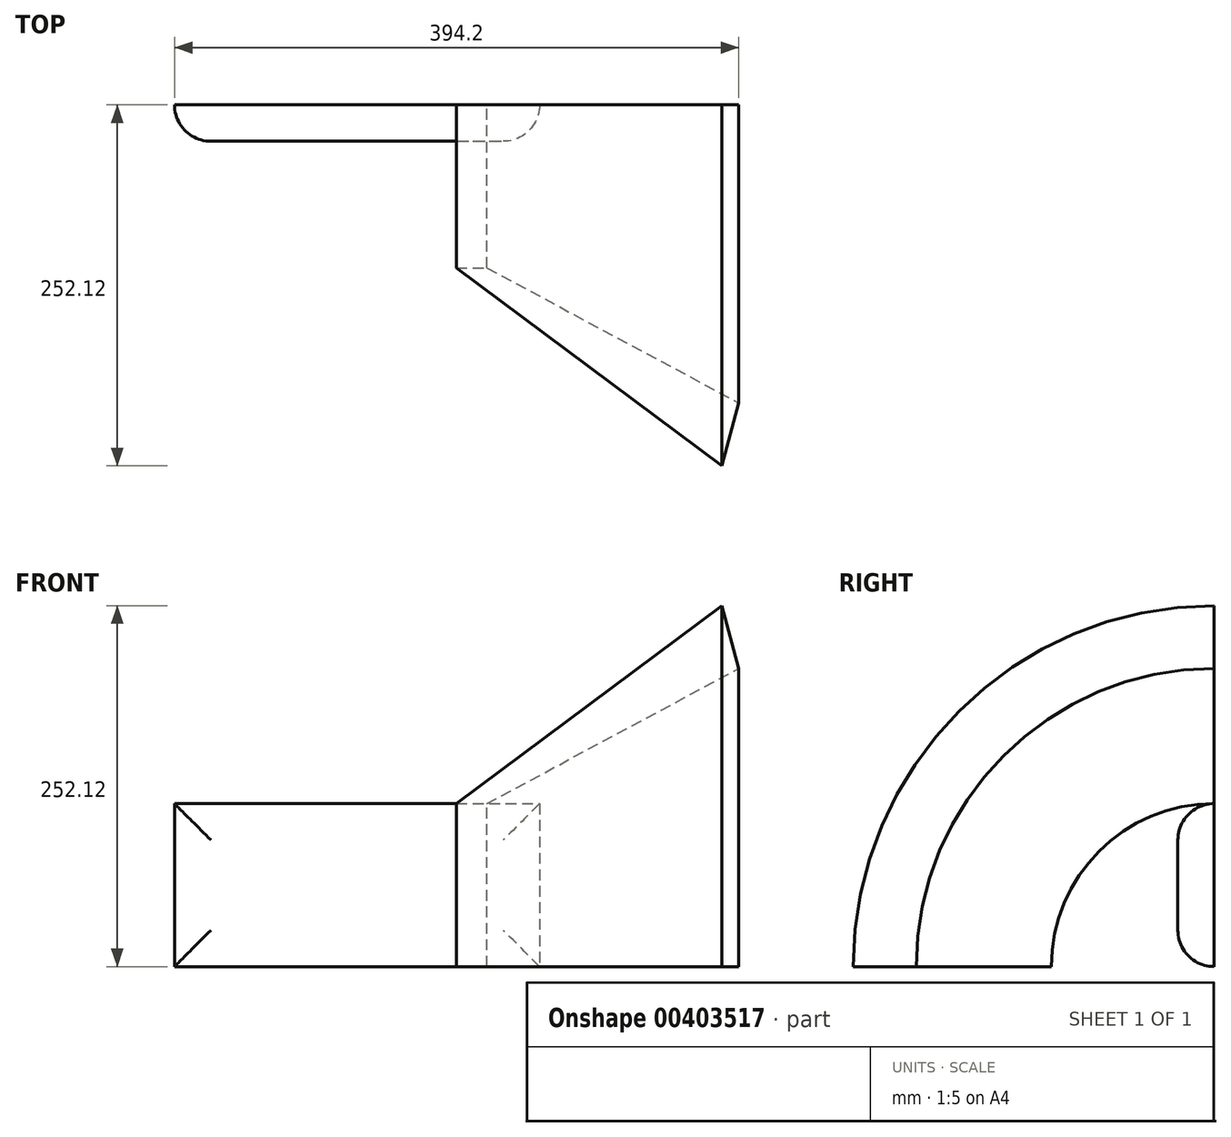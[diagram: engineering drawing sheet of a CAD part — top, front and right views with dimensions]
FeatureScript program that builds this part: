
annotation { "Feature Type Name" : "Feature", "Feature Type Description" : "" }
export const myFeature = defineFeature(function(context is Context, id is Id, definition is map)
    precondition{}
    {
        {
            var Q0;
            Q0=qCreatedBy(makeId("Front.planeOp"),FACE);
            var sketch = newSketch(context, id + "F0", { "sketchPlane" : qUnion([Q0])});
            skLineSegment(sketch, "E0.bottom", {"start": v(-64.42, 72.6) * mm, "end": v(39.43, 72.6) * mm});
            skLineSegment(sketch, "E0.top", {"start": v(-64.42, -41.2) * mm, "end": v(39.43, -41.2) * mm});
            skLineSegment(sketch, "E0.left", {"start": v(-64.42, 72.6) * mm, "end": v(-64.42, -41.2) * mm});
            skLineSegment(sketch, "E0.right", {"start": v(39.43, 72.6) * mm, "end": v(39.43, -41.2) * mm});
            skSolve(sketch);
        }
        {
            var Q0;
            Q0=makeQuery(id+"F0.imprint","IMPRINT",FACE,{"disambiguationData":[TD([[makeQuery(id+"F0.imprint","IMPRINT",EDGE,{"derivedFrom":sQuery(id+"F0.wireOp",EDGE,"E0.bottom")}),-1.0]])]});
            extrude(context, id + "F1", {"entities" : qUnion([Q0]), "depth" : 25.4 * mm});
        }
        {
            var Q0;
            Q0=makeQuery(id+"F1.opExtrude","SWEPT_FACE",FACE,{"disambiguationData":[OSD([sQuery(id+"F0.wireOp",EDGE,"E0.left")])]});
            extrude(context, id + "F2", {"entities" : qUnion([Q0]), "operationType" : NewBodyOperationType.ADD, "depth" : 151.21 * mm});
        }
        {
            var Q0;
            {var subQ0=sQuery(id+"F0.wireOp",EDGE,"E0.left");Q0=makeQuery(id+"F2.opExtrude","CAP_EDGE",EDGE,{"disambiguationData":[OSD([subQ0]),TDD([makeQuery(id+"F1.opExtrude","CAP_EDGE",EDGE,{"disambiguationData":[OSD([subQ0])],"isStart":false})])],"isStart":false});}
            var Q1;
            {var subQ0=sQuery(id+"F0.wireOp",EDGE,"E0.left");var subQ1=sQuery(id+"F0.wireOp",EDGE,"E0.bottom");Q1=makeQuery(id+"F2.boolean.opBoolean","MERGE",EDGE,{"derivedFrom":[makeQuery(id+"F1.opExtrude","CAP_EDGE",EDGE,{"disambiguationData":[OSD([subQ1])],"isStart":false}),makeQuery(id+"F2.opExtrude","SWEPT_EDGE",EDGE,{"disambiguationData":[OSD([subQ1,subQ0]),TDD([makeQuery(id+"F1.opExtrude","CAP_VERTEX",VERTEX,{"disambiguationData":[OSD([subQ1,subQ0])],"isStart":false})])]})]});}
            var Q2;
            {var subQ0=sQuery(id+"F0.wireOp",EDGE,"E0.left");var subQ1=sQuery(id+"F0.wireOp",EDGE,"E0.top");Q2=makeQuery(id+"F2.boolean.opBoolean","MERGE",EDGE,{"derivedFrom":[makeQuery(id+"F1.opExtrude","CAP_EDGE",EDGE,{"disambiguationData":[OSD([subQ1])],"isStart":false}),makeQuery(id+"F2.opExtrude","SWEPT_EDGE",EDGE,{"disambiguationData":[OSD([subQ1,subQ0]),TDD([makeQuery(id+"F1.opExtrude","CAP_VERTEX",VERTEX,{"disambiguationData":[OSD([subQ1,subQ0])],"isStart":false})])]})]});}
            var Q3;
            Q3=makeQuery(id+"F1.opExtrude","CAP_EDGE",EDGE,{"disambiguationData":[OSD([sQuery(id+"F0.wireOp",EDGE,"E0.right")])],"isStart":false});
            fillet(context, id + "F3", {"entities" : qUnion([Q0, Q1, Q2, Q3]), "radius" : 25.4 * mm, "tangentPropagation" : true, "allowEdgeOverflow" : false});
        }
        {
            var Q0;
            {var subQ0=sQuery(id+"F0.wireOp",EDGE,"E0.left");Q0=makeQuery(id+"F2.boolean.opBoolean","MERGE",FACE,{"derivedFrom":[makeQuery(id+"F1.opExtrude","CAP_FACE",FACE,{"disambiguationData":[OSD([sQuery(id+"F0.wireOp",EDGE,"E0.bottom"),sQuery(id+"F0.wireOp",EDGE,"E0.top"),subQ0,sQuery(id+"F0.wireOp",EDGE,"E0.right")])],"isStart":true}),makeQuery(id+"F2.opExtrude","SWEPT_FACE",FACE,{"disambiguationData":[OSD([subQ0]),TDD([makeQuery(id+"F1.opExtrude","CAP_EDGE",EDGE,{"disambiguationData":[OSD([subQ0])],"isStart":true})])]})]});}
            var sketch = newSketch(context, id + "F4", { "sketchPlane" : qUnion([Q0])});
            skLineSegment(sketch, "E1", {"start": v(-166.8, 210.91) * mm, "end": v(73.42, 31.84) * mm});
            skLineSegment(sketch, "E2", {"start": v(73.42, 31.84) * mm, "end": v(-178.57, 166.97) * mm});
            skLineSegment(sketch, "E3", {"start": v(-178.57, 166.97) * mm, "end": v(-166.8, 210.91) * mm});
            skSolve(sketch);
        }
        {
            var Q0;
            {var subQ0=sQuery(id+"F4.wireOp",EDGE,"E3");Q0=makeQuery(id+"F4.imprint","IMPRINT",FACE,{"disambiguationData":[TD([[makeQuery(id+"F4.imprint","IMPRINT",EDGE,{"derivedFrom":subQ0}),-1.0]])]});}
            var Q1;
            {var subQ0=sQuery(id+"F0.wireOp",EDGE,"E0.left");var subQ1=sQuery(id+"F0.wireOp",EDGE,"E0.top");Q1=makeQuery(id+"F3.opFillet","BLEND_EDGE",EDGE,{"blendedFrom":[makeQuery(id+"F2.boolean.opBoolean","MERGE",EDGE,{"derivedFrom":[makeQuery(id+"F1.opExtrude","CAP_EDGE",EDGE,{"disambiguationData":[OSD([subQ1])],"isStart":false}),makeQuery(id+"F2.opExtrude","SWEPT_EDGE",EDGE,{"disambiguationData":[OSD([subQ1,subQ0]),TDD([makeQuery(id+"F1.opExtrude","CAP_VERTEX",VERTEX,{"disambiguationData":[OSD([subQ1,subQ0])],"isStart":false})])]})]}),makeQuery(id+"F2.boolean.opBoolean","MERGE",FACE,{"derivedFrom":[makeQuery(id+"F1.opExtrude","CAP_FACE",FACE,{"disambiguationData":[OSD([sQuery(id+"F0.wireOp",EDGE,"E0.bottom"),subQ1,subQ0,sQuery(id+"F0.wireOp",EDGE,"E0.right")])],"isStart":true}),makeQuery(id+"F2.opExtrude","SWEPT_FACE",FACE,{"disambiguationData":[OSD([subQ0]),TDD([makeQuery(id+"F1.opExtrude","CAP_EDGE",EDGE,{"disambiguationData":[OSD([subQ0])],"isStart":true})])]})]})],"blendedInto":[makeQuery(id+"F2.boolean.opBoolean","MERGE",FACE,{"derivedFrom":[makeQuery(id+"F1.opExtrude","CAP_FACE",FACE,{"disambiguationData":[OSD([sQuery(id+"F0.wireOp",EDGE,"E0.bottom"),subQ1,subQ0,sQuery(id+"F0.wireOp",EDGE,"E0.right")])],"isStart":true}),makeQuery(id+"F2.opExtrude","SWEPT_FACE",FACE,{"disambiguationData":[OSD([subQ0]),TDD([makeQuery(id+"F1.opExtrude","CAP_EDGE",EDGE,{"disambiguationData":[OSD([subQ0])],"isStart":true})])]})]})]});}
            revolve(context, id + "F5", {"entities" : qUnion([Q0]), "axis" : qUnion([Q1]), "revolveType" : RevolveType.ONE_DIRECTION, "angle" : 90 * degree});
        }
    });
